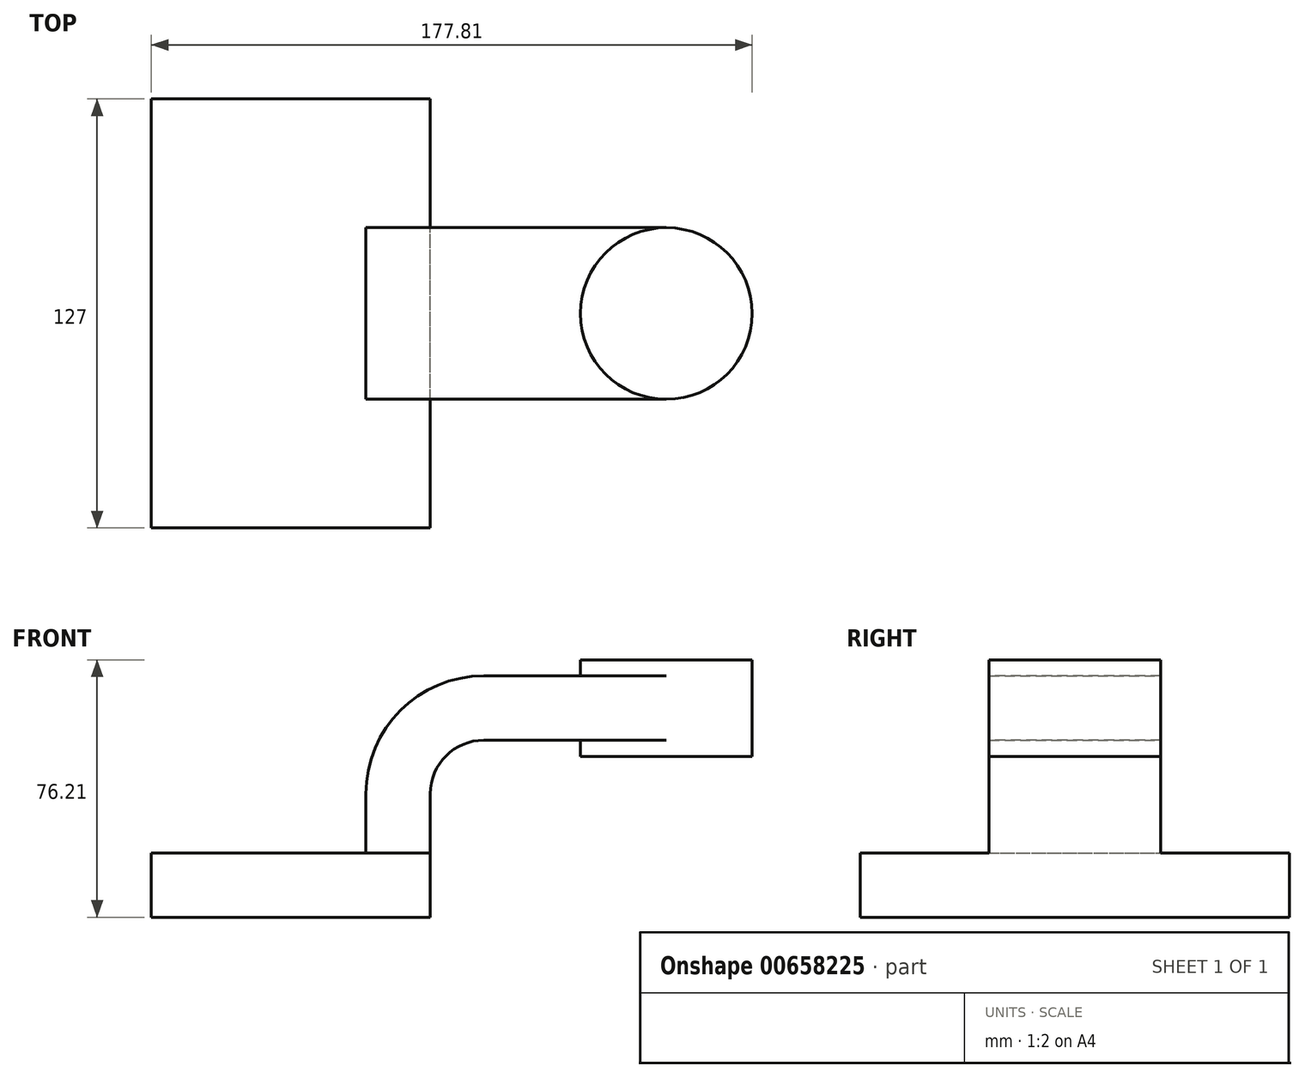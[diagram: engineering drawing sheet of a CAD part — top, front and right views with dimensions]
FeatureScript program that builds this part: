
annotation { "Feature Type Name" : "Feature", "Feature Type Description" : "" }
export const myFeature = defineFeature(function(context is Context, id is Id, definition is map)
    precondition{}
    {
        {
            var Q0;
            Q0=qCreatedBy(makeId("Front.planeOp"),FACE);
            var sketch = newSketch(context, id + "F0", { "sketchPlane" : qUnion([Q0])});
            skLineSegment(sketch, "E0.bottom", {"start": v(-41.28, 9.52) * mm, "end": v(41.27, 9.53) * mm});
            skLineSegment(sketch, "E0.top", {"start": v(-41.28, -9.53) * mm, "end": v(41.28, -9.53) * mm});
            skLineSegment(sketch, "E0.left", {"start": v(-41.28, 9.52) * mm, "end": v(-41.27, -9.53) * mm});
            skLineSegment(sketch, "E0.right", {"start": v(41.28, 9.53) * mm, "end": v(41.28, -9.52) * mm});
            skPoint(sketch, "E0.middle", {"position": v(0, 0) * mm});
            skLineSegment(sketch, "E1.bottom", {"start": v(85.73, 38.1) * mm, "end": v(136.53, 38.1) * mm});
            skLineSegment(sketch, "E1.top", {"start": v(85.73, 66.67) * mm, "end": v(136.53, 66.67) * mm});
            skLineSegment(sketch, "E1.left", {"start": v(85.73, 38.1) * mm, "end": v(85.73, 66.67) * mm});
            skLineSegment(sketch, "E1.right", {"start": v(136.53, 38.1) * mm, "end": v(136.53, 66.67) * mm});
            skPoint(sketch, "E1.middle", {"position": v(111.12, 52.39) * mm});
            skLineSegment(sketch, "E2", {"start": v(41.27, 9.53) * mm, "end": v(41.27, 27) * mm});
            skArc(sketch, "E3", {"start": v(41.27, 27) * mm, "mid": v(45.92, 38.23) * mm, "end": v(57.15, 42.88) * mm});
            skLineSegment(sketch, "E4", {"start": v(57.15, 42.88) * mm, "end": v(111.12, 42.88) * mm});
            skLineSegment(sketch, "E5.0", {"start": v(57.15, 61.93) * mm, "end": v(111.12, 61.93) * mm});
            skArc(sketch, "E5.1", {"start": v(22.23, 27) * mm, "mid": v(32.45, 51.7) * mm, "end": v(57.15, 61.93) * mm});
            skLineSegment(sketch, "E5.2", {"start": v(22.22, 9.53) * mm, "end": v(22.22, 27) * mm});
            skLineSegment(sketch, "E6", {"start": v(111.12, 66.67) * mm, "end": v(111.12, 38.1) * mm});
            skFitSpline(sketch, "E7", {"points": [v(-41.28, 9.52) * mm, v(57.15, 61.93) * mm], "startDerivative": vector(0, 101.04) * mm, "endDerivative": vector(153.64, -31.23) * mm});
            skSolve(sketch);
        }
        {
            var Q0;
            Q0=makeQuery(id+"F0.imprint","IMPRINT",FACE,{"disambiguationData":[TD([[makeQuery(id+"F0.imprint","IMPRINT",EDGE,{"derivedFrom":sQuery(id+"F0.wireOp",EDGE,"E0.top")}),1.0]])]});
            extrude(context, id + "F1", {"entities" : qUnion([Q0]), "endBound" : BoundingType.SYMMETRIC, "depth" : 127 * mm, "offsetDistance" : 25.4 * mm});
        }
        {
            var Q0;
            {var subQ1=sQuery(id+"F0.wireOp",EDGE,"E2");Q0=makeQuery(id+"F0.imprint","IMPRINT",FACE,{"disambiguationData":[TD([[makeQuery(id+"F0.imprint","IMPRINT",EDGE,{"derivedFrom":subQ1}),1.0]])]});}
            var Q1;
            {var subQ0=sQuery(id+"F0.wireOp",EDGE,"E4");var subQ1=sQuery(id+"F0.wireOp",EDGE,"E1.left");var subQ2=makeQuery(id+"F0.imprint","INTERSECT",VERTEX,{"derivedFrom":[subQ1,subQ0]});Q1=makeQuery(id+"F0.imprint","IMPRINT",FACE,{"disambiguationData":[TD([[makeQuery(id+"F0.imprint","IMPRINT",EDGE,{"disambiguationData":[TD([[subQ2,-1.0]])],"derivedFrom":subQ1}),-1.0]])]});}
            extrude(context, id + "F2", {"entities" : qUnion([Q0, Q1]), "operationType" : NewBodyOperationType.ADD, "endBound" : BoundingType.SYMMETRIC, "depth" : 50.8 * mm, "offsetDistance" : 25.4 * mm});
        }
        {
            var Q0;
            Q0=makeQuery(id+"F0.imprint","IMPRINT",FACE,{"disambiguationData":[TD([[makeQuery(id+"F0.imprint","IMPRINT",EDGE,{"derivedFrom":sQuery(id+"F0.wireOp",EDGE,"E5.1")}),1.0]])]});
            extrude(context, id + "F3", {"entities" : qUnion([Q0]), "operationType" : NewBodyOperationType.ADD, "endBound" : BoundingType.SYMMETRIC, "depth" : 15.88 * mm, "offsetDistance" : 25.4 * mm});
        }
        {
            var Q0;
            {var subQ0=sQuery(id+"F0.wireOp",EDGE,"E1.right");Q0=makeQuery(id+"F0.imprint","IMPRINT",FACE,{"disambiguationData":[TD([[makeQuery(id+"F0.imprint","IMPRINT",EDGE,{"derivedFrom":subQ0}),1.0]])]});}
            var Q1;
            Q1=sQuery(id+"F0.wireOp",EDGE,"E6");
            revolve(context, id + "F4", {"operationType" : NewBodyOperationType.ADD, "entities" : qUnion([Q0]), "axis" : qUnion([Q1]), "revolveType" : RevolveType.FULL});
        }
        {
            var Q0;
            Q0=makeQuery(id+"F1.opExtrude","SWEPT_BODY",BODY,{"disambiguationData":[OSD([sQuery(id+"F0.wireOp",EDGE,"E0.bottom"),sQuery(id+"F0.wireOp",EDGE,"E0.top"),sQuery(id+"F0.wireOp",EDGE,"E0.left"),sQuery(id+"F0.wireOp",EDGE,"E0.right")])]});
            transform(context, id + "F5", {"entities" : qUnion([Q0]), "transformType" : TransformType.TRANSLATION_3D, "dx" : 0 * mm, "dy" : 0 * mm, "dz" : 0 * mm, "makeCopy" : true});
        }
        {
            var Q0;
            Q0=makeQuery(id+"F1.opExtrude","SWEPT_BODY",BODY,{"disambiguationData":[OSD([sQuery(id+"F0.wireOp",EDGE,"E0.bottom"),sQuery(id+"F0.wireOp",EDGE,"E0.top"),sQuery(id+"F0.wireOp",EDGE,"E0.left"),sQuery(id+"F0.wireOp",EDGE,"E0.right")])]});
            transform(context, id + "F6", {"entities" : qUnion([Q0]), "transformType" : TransformType.TRANSLATION_3D, "dx" : 50.8 * mm, "dy" : 50.8 * mm, "dz" : 50.8 * mm, "makeCopy" : true});
        }
        {
            var Q0;
            Q0=makeQuery(id+"F5.opPattern","COPY",BODY,{"derivedFrom":makeQuery(id+"F1.opExtrude","SWEPT_BODY",BODY,{"disambiguationData":[OSD([sQuery(id+"F0.wireOp",EDGE,"E0.bottom"),sQuery(id+"F0.wireOp",EDGE,"E0.top"),sQuery(id+"F0.wireOp",EDGE,"E0.left"),sQuery(id+"F0.wireOp",EDGE,"E0.right")])]}),"instanceName":"1"});
            deleteBodies(context, id + "F7", {"entities" : qUnion([Q0])});
        }
        {
            var Q0;
            Q0=makeQuery(id+"F6.opPattern","COPY",BODY,{"derivedFrom":makeQuery(id+"F1.opExtrude","SWEPT_BODY",BODY,{"disambiguationData":[OSD([sQuery(id+"F0.wireOp",EDGE,"E0.bottom"),sQuery(id+"F0.wireOp",EDGE,"E0.top"),sQuery(id+"F0.wireOp",EDGE,"E0.left"),sQuery(id+"F0.wireOp",EDGE,"E0.right")])]}),"instanceName":"1"});
            deleteBodies(context, id + "F8", {"entities" : qUnion([Q0])});
        }
    });
